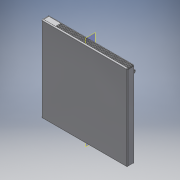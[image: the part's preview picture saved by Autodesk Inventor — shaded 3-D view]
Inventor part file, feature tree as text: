
AUTODESK INVENTOR PART (.ipt)
format: ipt  version: 2018 (Build 220112000, 112)  size: 471,552 bytes
history: native  units: in
note: dims shown in document units (in); Inventor stores cm internally (conversion verified against a paired STEP export)
features: reference x11, sketch x8, extrude x8, fillet x8, plane x3, other x3, thread x2, mirror x1
ambient origin geometry x8: Origin, YZ Plane, XZ Plane, XY Plane, X Axis, Y Axis, Z Axis, Center Point
bodies: Solid1 (feature_tree)
feature tree (44):
  sketch  "Sketch1"  dims[d0=1.0in d1=0.0in d2=0.2in d3=0.0in]
  plane  "Work Plane1"
  extrude  "Extrusion1"  Depth=0.2in TaperAngle=0.0deg
  extrude  "Extrusion2"  Depth=0.25in
  sketch  "Sketch3"  dims[d7=0.175in d8=0.175in]
  plane  "Work Plane2"
  extrude  "Extrusion3"  Depth=0.175in
  extrude  "Extrusion4"  Depth=0.025in
  fillet  "Fillet1"  Radius=0.1in
  fillet  "Fillet2"  Radius=0.1in
  thread  "Thread1"  [1 undecoded]
  plane  "Work Plane3"
  mirror  "Mirror1"
  fillet  "Fillet3"  Radius=1.0in
  fillet  "Fillet4"  Radius=0.1in
  thread  "Thread2"  [1 undecoded]
  extrude  "Extrusion5"  Depth=0.175in
  fillet  "Fillet5"  Radius=0.0875in
  fillet  "Fillet6"  Radius=0.0875in
  extrude  "Extrusion6"  Depth=0.1in TaperAngle=0.0deg
  fillet  "Fillet7"  Radius=0.1in
  extrude  "Extrusion7"  Depth=0.1in TaperAngle=0.0deg
  fillet  "Fillet8"  Radius=0.05in
  extrude  "Extrusion8"  Depth=0.025in
  reference  "Reference1"
  sketch  "Sketch2"  dims[d4=0.2in d5=0.0in d6=0.25in]
  reference  "Reference2"
  reference  "Reference3"
  reference  "Reference4"
  reference  "Reference5"
  reference  "Reference6"
  reference  "Reference7"
  reference  "Reference8"
  reference  "Reference9"
  reference  "Reference10"
  sketch  "Sketch4"  dims[d9=0.125in d10=0.0925in d11=0.1in d12=0.0in d13=0.1in d14=0.025in d15=1.0in d16=0.0in d17=0.1in d18=0.025in]
  reference  "Reference11"
  sketch  "Sketch5"  dims[d19=1.0in d20=0.0in d21=0.175in d22=0.0875in d23=0.0875in]
  sketch  "Sketch6"  dims[d24=0.125in d25=0.1in d26=0.0in d27=0.1in]
  sketch  "Sketch7"  dims[d28=0.025in d29=0.1in d30=0.0in d31=0.05in]
  sketch  "Sketch8"  dims[d33=0.75in d34=0.025in d35=0.025in d36=0.025in d37=0.025in d38=0.025in d39=0.025in d40=0.025in d41=0.025in d42=0.025in d43=0.025in d44=0.025in d45=0.025in d46=0.0in d47=0.05in d48=0.025in d49=0.025in d50=0.005in d51=0.0in]
  other  "<userpath>\Documents\Commodore Cube Project\Case\Assembly.iam"
  other  "Assembly.iam"
  other  "Tray:1"
note: 2 required parameter values undecoded (feature->parameter linkage not recoverable at this tier; creation-order binding heuristic only, values carry confidence <= 0.55)
